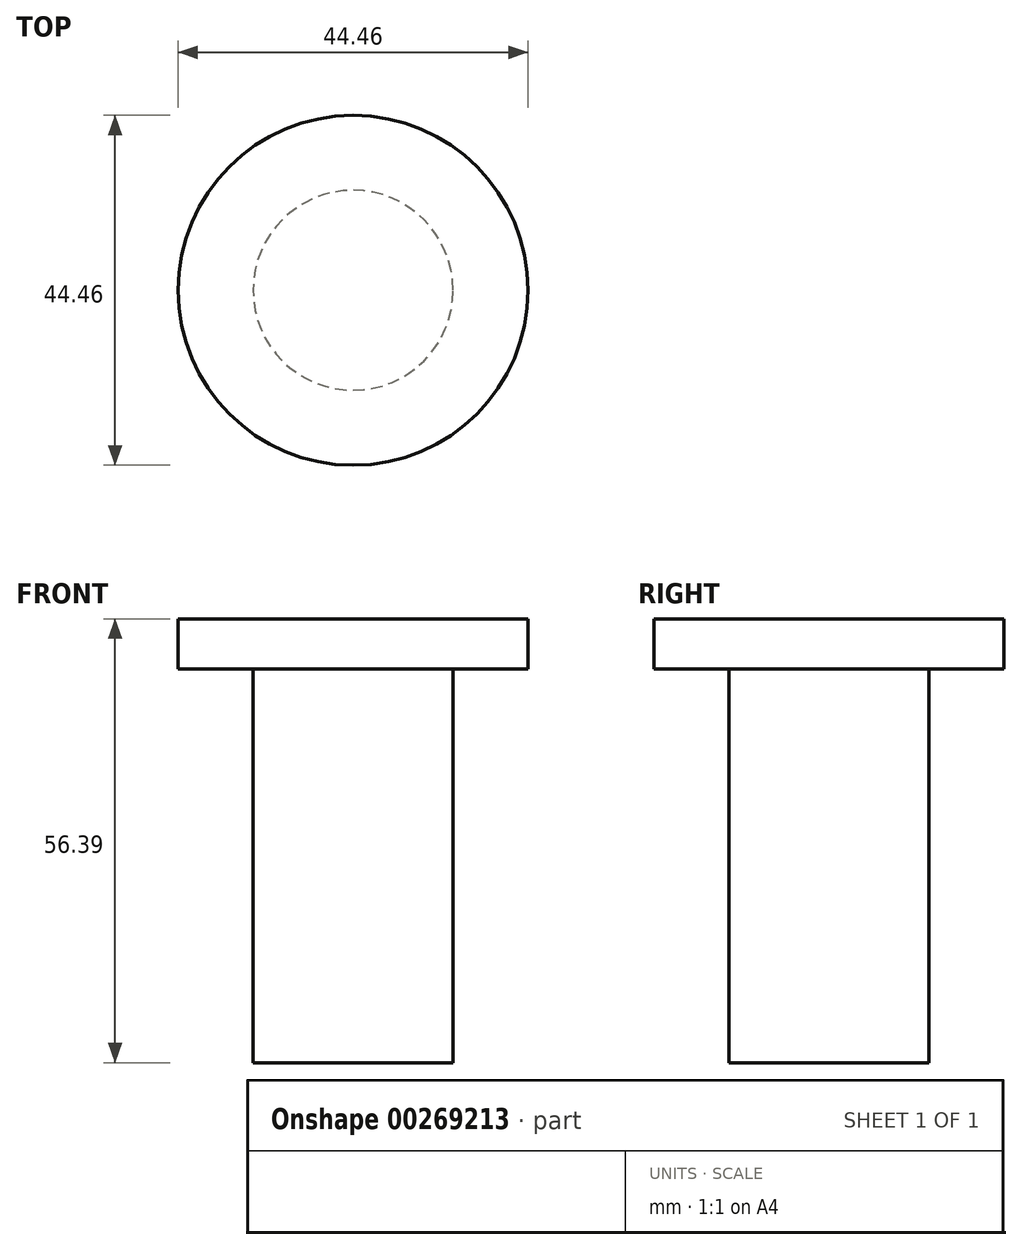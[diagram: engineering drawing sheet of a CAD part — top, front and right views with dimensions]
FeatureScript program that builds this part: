
annotation { "Feature Type Name" : "Feature", "Feature Type Description" : "" }
export const myFeature = defineFeature(function(context is Context, id is Id, definition is map)
    precondition{}
    {
        {
            var Q0;
            Q0=qCreatedBy(makeId("Top.planeOp"),FACE);
            var sketch = newSketch(context, id + "F0", { "sketchPlane" : qUnion([Q0])});
            skCircle(sketch, "E0", {"center": v(0, 0) * mm, "radius": 12.7 * mm});
            skSolve(sketch);
        }
        {
            var Q0;
            Q0 = qSketchRegion(id + "F0", true);
            extrude(context, id + "F1", {"entities" : qUnion([Q0]), "depth" : 50.8 * mm});
        }
        {
            var Q0;
            Q0=qCreatedBy(makeId("Top.planeOp"),FACE);
            cPlane(context, id + "F2", {"entities" : qUnion([Q0]), "cplaneType" : CPlaneType.OFFSET, "offset" : 50.04 * mm, "width" : 152.4 * mm, "height" : 152.4 * mm});
        }
        {
            var Q0;
            Q0=qCreatedBy(id+"F2.planeOp",FACE);
            var sketch = newSketch(context, id + "F3", { "sketchPlane" : qUnion([Q0])});
            skCircle(sketch, "E1", {"center": v(0, 0) * mm, "radius": 22.23 * mm});
            skSolve(sketch);
        }
        {
            var Q0;
            Q0 = qSketchRegion(id + "F3", true);
            extrude(context, id + "F4", {"entities" : qUnion([Q0]), "operationType" : NewBodyOperationType.ADD, "depth" : 6.35 * mm});
        }
    });
